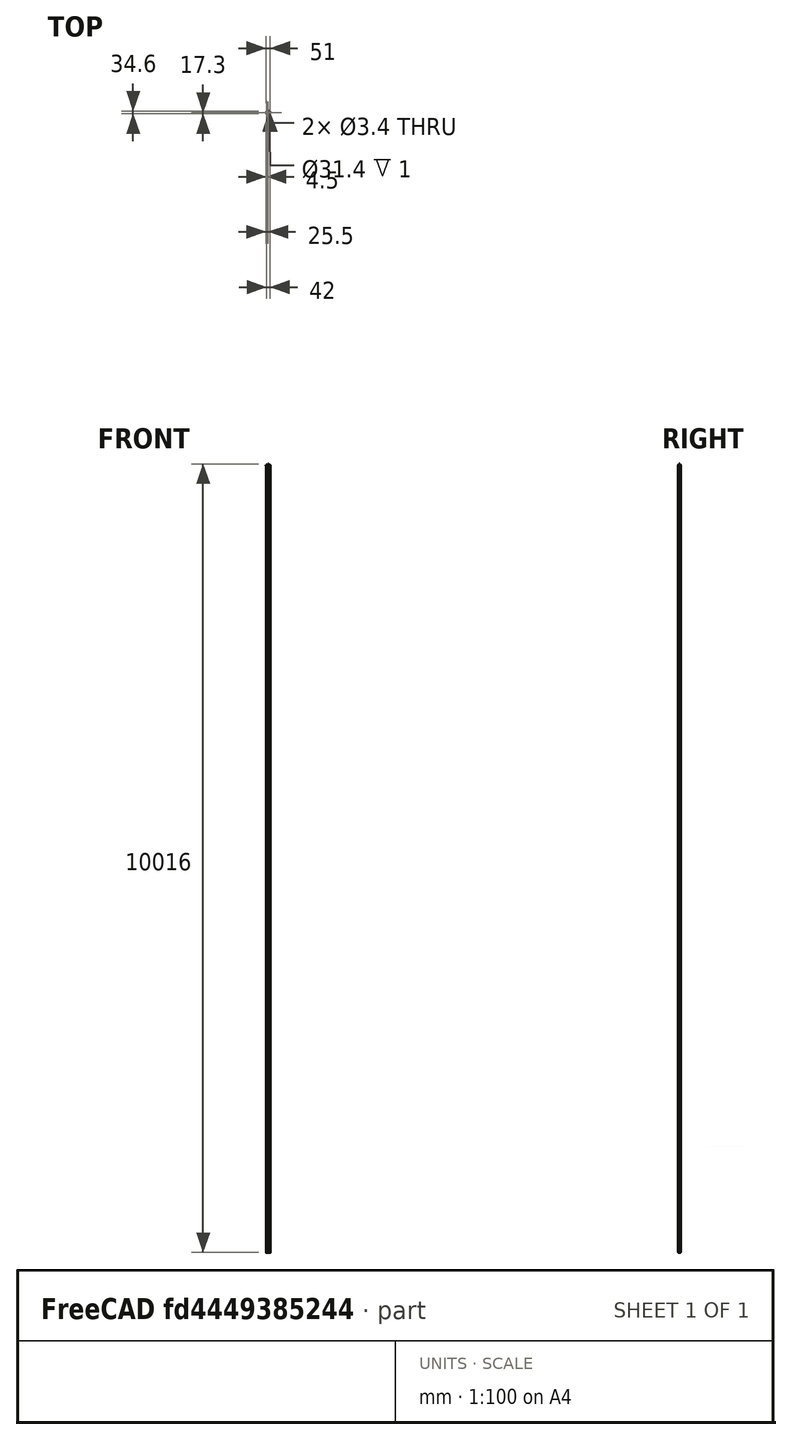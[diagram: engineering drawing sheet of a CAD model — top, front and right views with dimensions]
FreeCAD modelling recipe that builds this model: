
FCSTD DOCUMENT  (FreeCAD 0.15R4671 (Git))
Label: Small Stepper Test Frame
License: All rights reserved
LicenseURL: http://en.wikipedia.org/wiki/All_rights_reserved
objects: Sketcher::SketchObject×7, PartDesign::Pocket×4, PartDesign::Pad×3, Mesh::Feature×1
note: 21 computed .brp shape members not serialized (recipe doc carries the construction recipe); baked Part::Feature solids carry a one-line shape summary decoded from their .brp

FEATURE [Sketcher::SketchObject] Sketch
  sketch-geometry (11):
    g0: Circle [constr] CenterX=0 CenterY=0 CenterZ=0 NormalX=0 NormalY=0 NormalZ=1 Radius=13.5
    g1: Circle [constr] CenterX=-21 CenterY=0 CenterZ=0 NormalX=0 NormalY=0 NormalZ=1 Radius=4.5
    g2: Circle [constr] CenterX=21 CenterY=0 CenterZ=0 NormalX=0 NormalY=0 NormalZ=1 Radius=4.5
    g3: LineSegment StartX=-22.9286 StartY=4.06578 StartZ=0 EndX=-5.78572 EndY=12.1974 EndZ=0
    g4: LineSegment StartX=5.78572 StartY=12.1974 StartZ=0 EndX=22.9286 EndY=4.06578 EndZ=0
    g5: LineSegment StartX=22.9286 StartY=-4.06578 StartZ=0 EndX=5.78572 EndY=-12.1974 EndZ=0
    g6: LineSegment StartX=-5.78572 StartY=-12.1974 StartZ=0 EndX=-22.9286 EndY=-4.06578 EndZ=0
    g7: ArcOfCircle CenterX=-21 CenterY=0 CenterZ=0 NormalX=0 NormalY=0 NormalZ=1 Radius=4.5 StartAngle=2.01371 EndAngle=4.26947
    g8: ArcOfCircle CenterX=0 CenterY=0 CenterZ=0 NormalX=0 NormalY=0 NormalZ=1 Radius=13.5 StartAngle=1.12788 EndAngle=2.01371
    g9: ArcOfCircle CenterX=21 CenterY=0 CenterZ=0 NormalX=0 NormalY=0 NormalZ=1 Radius=4.5 StartAngle=5.15531 EndAngle=7.41107
    g10: ArcOfCircle CenterX=0 CenterY=0 CenterZ=0 NormalX=0 NormalY=0 NormalZ=1 Radius=13.5 StartAngle=4.26948 EndAngle=5.1553
  constraints (36):
    c: Coincident(g0,g-1)
    c: PointOnObject(g1,g-1)
    c: PointOnObject(g2,g-1)
    c: Symmetric(g1,g2,g-2)
    c: Equal(g1,g2)
    c: Radius(g0) = 13.5
    c: DistanceX(g1,g2) = 42
    c: Radius(g2) = 4.5
    c: PointOnObject(g3,g1)
    c: PointOnObject(g3,g0)
    c: Tangent(g3,g1)
    c: PointOnObject(g4,g0)
    c: PointOnObject(g4,g2)
    c: Tangent(g4,g2)
    c: PointOnObject(g5,g2)
    c: Tangent(g5,g0)
    c: PointOnObject(g6,g0)
    c: PointOnObject(g6,g1)
    c: Tangent(g6,g1)
    c: Tangent(g3,g0)
    c: Tangent(g4,g0)
    c: Tangent(g5,g2)
    c: Tangent(g6,g0)
    c: PointOnObject(g5,g0)
    c: Coincident(g7,g1)
    c: Coincident(g7,g3)
    c: Coincident(g7,g6)
    c: Coincident(g8,g-1)
    c: Coincident(g8,g3)
    c: Coincident(g8,g4)
    c: Coincident(g9,g2)
    c: Coincident(g9,g4)
    c: Coincident(g9,g5)
    c: Coincident(g10,g-1)
    c: Coincident(g10,g5)
    c: Coincident(g10,g6)
FEATURE [PartDesign::Pad] Pad
  Length = 2
  Length2 = 100
  Sketch = -> Sketch
  Type = 0
FEATURE [Sketcher::SketchObject] Sketch001
  Placement = pos=(0,0,2) rot=(0,0,1;0rad)
  Support = -> Pad [Face10]
  sketch-geometry (11):
    g0: Circle [constr] CenterX=0 CenterY=0 CenterZ=0 NormalX=0 NormalY=0 NormalZ=1 Radius=12.7
    g1: Circle [constr] CenterX=-21 CenterY=0 CenterZ=0 NormalX=0 NormalY=0 NormalZ=1 Radius=3.7
    g2: Circle [constr] CenterX=21 CenterY=0 CenterZ=0 NormalX=0 NormalY=0 NormalZ=1 Radius=3.7
    g3: LineSegment StartX=-22.5857 StartY=3.34297 StartZ=0 EndX=-5.44286 EndY=11.4745 EndZ=0
    g4: LineSegment StartX=5.44286 StartY=11.4745 StartZ=0 EndX=22.5857 EndY=3.34297 EndZ=0
    g5: LineSegment StartX=22.5857 StartY=-3.34297 StartZ=0 EndX=5.44286 EndY=-11.4745 EndZ=0
    g6: LineSegment StartX=-5.44286 StartY=-11.4745 StartZ=0 EndX=-22.5857 EndY=-3.34297 EndZ=0
    g7: ArcOfCircle CenterX=-21 CenterY=0 CenterZ=0 NormalX=0 NormalY=0 NormalZ=1 Radius=3.7 StartAngle=2.01371 EndAngle=4.26947
    g8: ArcOfCircle CenterX=0 CenterY=0 CenterZ=0 NormalX=0 NormalY=0 NormalZ=1 Radius=12.7 StartAngle=1.12788 EndAngle=2.01371
    g9: ArcOfCircle CenterX=21 CenterY=0 CenterZ=0 NormalX=0 NormalY=0 NormalZ=1 Radius=3.7 StartAngle=5.1553 EndAngle=7.41107
    g10: ArcOfCircle CenterX=0 CenterY=0 CenterZ=0 NormalX=0 NormalY=0 NormalZ=1 Radius=12.7 StartAngle=4.26948 EndAngle=5.1553
  constraints (36):
    c: Coincident(g0,g-1)
    c: PointOnObject(g1,g-1)
    c: PointOnObject(g2,g-1)
    c: Symmetric(g1,g2,g-2)
    c: Equal(g1,g2)
    c: Radius(g0) = 12.7
    c: DistanceX(g1,g2) = 42
    c: Radius(g2) = 3.7
    c: PointOnObject(g3,g1)
    c: PointOnObject(g3,g0)
    c: Tangent(g3,g1)
    c: PointOnObject(g4,g0)
    c: PointOnObject(g4,g2)
    c: Tangent(g4,g2)
    c: PointOnObject(g5,g2)
    c: Tangent(g5,g0)
    c: PointOnObject(g6,g0)
    c: PointOnObject(g6,g1)
    c: Tangent(g6,g1)
    c: Tangent(g3,g0)
    c: Tangent(g4,g0)
    c: Tangent(g5,g2)
    c: Tangent(g6,g0)
    c: PointOnObject(g5,g0)
    c: Coincident(g7,g1)
    c: Coincident(g7,g3)
    c: Coincident(g7,g6)
    c: Coincident(g8,g-1)
    c: Coincident(g8,g3)
    c: Coincident(g8,g4)
    c: Coincident(g9,g2)
    c: Coincident(g9,g4)
    c: Coincident(g9,g5)
    c: Coincident(g10,g-1)
    c: Coincident(g10,g5)
    c: Coincident(g10,g6)
FEATURE [PartDesign::Pocket] Pocket
  Length = 1
  Sketch = -> Sketch001
  Type = 0
FEATURE [Sketcher::SketchObject] Sketch002
  Placement = pos=(0,0,1) rot=(0,0,1;0rad)
  Support = -> Pocket [Face19]
  sketch-geometry (11):
    g0: Circle [constr] CenterX=0 CenterY=0 CenterZ=0 NormalX=0 NormalY=0 NormalZ=1 Radius=11.7
    g1: Circle [constr] CenterX=-21 CenterY=0 CenterZ=0 NormalX=0 NormalY=0 NormalZ=1 Radius=2.7
    g2: Circle [constr] CenterX=21 CenterY=0 CenterZ=0 NormalX=0 NormalY=0 NormalZ=1 Radius=2.7
    g3: LineSegment StartX=-22.1571 StartY=2.43947 StartZ=0 EndX=-5.01426 EndY=10.5711 EndZ=0
    g4: LineSegment StartX=5.01426 StartY=10.5711 StartZ=0 EndX=22.1571 EndY=2.43947 EndZ=0
    g5: LineSegment StartX=22.1571 StartY=-2.43947 StartZ=0 EndX=5.01426 EndY=-10.5711 EndZ=0
    g6: LineSegment StartX=-5.01426 StartY=-10.5711 StartZ=0 EndX=-22.1571 EndY=-2.43947 EndZ=0
    g7: ArcOfCircle CenterX=-21 CenterY=0 CenterZ=0 NormalX=0 NormalY=0 NormalZ=1 Radius=2.7 StartAngle=2.01371 EndAngle=4.26948
    g8: ArcOfCircle CenterX=0 CenterY=0 CenterZ=0 NormalX=0 NormalY=0 NormalZ=1 Radius=11.7 StartAngle=1.12789 EndAngle=2.01371
    g9: ArcOfCircle CenterX=21 CenterY=0 CenterZ=0 NormalX=0 NormalY=0 NormalZ=1 Radius=2.7 StartAngle=5.1553 EndAngle=7.41107
    g10: ArcOfCircle CenterX=0 CenterY=0 CenterZ=0 NormalX=0 NormalY=0 NormalZ=1 Radius=11.7 StartAngle=4.26948 EndAngle=5.1553
  constraints (36):
    c: Coincident(g0,g-1)
    c: PointOnObject(g1,g-1)
    c: PointOnObject(g2,g-1)
    c: Symmetric(g1,g2,g-2)
    c: Equal(g1,g2)
    c: Radius(g0) = 11.7
    c: DistanceX(g1,g2) = 42
    c: Radius(g2) = 2.7
    c: PointOnObject(g3,g1)
    c: PointOnObject(g3,g0)
    c: Tangent(g3,g1)
    c: PointOnObject(g4,g0)
    c: PointOnObject(g4,g2)
    c: Tangent(g4,g2)
    c: PointOnObject(g5,g2)
    c: Tangent(g5,g0)
    c: PointOnObject(g6,g0)
    c: PointOnObject(g6,g1)
    c: Tangent(g6,g1)
    c: Tangent(g3,g0)
    c: Tangent(g4,g0)
    c: Tangent(g5,g2)
    c: Tangent(g6,g0)
    c: PointOnObject(g5,g0)
    c: Coincident(g7,g1)
    c: Coincident(g7,g3)
    c: Coincident(g7,g6)
    c: Coincident(g8,g-1)
    c: Coincident(g8,g3)
    c: Coincident(g8,g4)
    c: Coincident(g9,g2)
    c: Coincident(g9,g4)
    c: Coincident(g9,g5)
    c: Coincident(g10,g-1)
    c: Coincident(g10,g5)
    c: Coincident(g10,g6)
FEATURE [PartDesign::Pocket] Pocket001
  Length = 5
  Sketch = -> Sketch002
  Type = 1
FEATURE [Sketcher::SketchObject] Sketch003
  sketch-geometry (14):
    g0: Circle [constr] CenterX=0 CenterY=0 CenterZ=0 NormalX=0 NormalY=0 NormalZ=1 Radius=17.3
    g1: Circle [constr] CenterX=-21 CenterY=0 CenterZ=0 NormalX=0 NormalY=0 NormalZ=1 Radius=3.3
    g2: Circle [constr] CenterX=21 CenterY=0 CenterZ=0 NormalX=0 NormalY=0 NormalZ=1 Radius=3.3
    g3: LineSegment StartX=-23.2 StartY=2.45967 StartZ=0 EndX=-11.5333 EndY=12.8947 EndZ=0
    g4: LineSegment StartX=11.5333 StartY=12.8947 StartZ=0 EndX=23.2 EndY=2.45968 EndZ=0
    g5: LineSegment StartX=23.2 StartY=-2.45968 StartZ=0 EndX=11.5333 EndY=-12.8947 EndZ=0
    g6: LineSegment StartX=-11.5333 StartY=-12.8947 StartZ=0 EndX=-23.2 EndY=-2.45967 EndZ=0
    g7: ArcOfCircle CenterX=-21 CenterY=0 CenterZ=0 NormalX=0 NormalY=0 NormalZ=1 Radius=3.3 StartAngle=2.30052 EndAngle=3.98266
    g8: ArcOfCircle CenterX=0 CenterY=0 CenterZ=0 NormalX=0 NormalY=0 NormalZ=1 Radius=17.3 StartAngle=0.841069 EndAngle=2.30052
    g9: ArcOfCircle CenterX=21 CenterY=0 CenterZ=0 NormalX=0 NormalY=0 NormalZ=1 Radius=3.3 StartAngle=5.44211 EndAngle=7.12426
    g10: ArcOfCircle CenterX=0 CenterY=0 CenterZ=0 NormalX=0 NormalY=0 NormalZ=1 Radius=17.3 StartAngle=3.98266 EndAngle=5.44212
    g11: Circle CenterX=-21 CenterY=0 CenterZ=0 NormalX=0 NormalY=0 NormalZ=1 Radius=1.7
    g12: Circle CenterX=21 CenterY=0 CenterZ=0 NormalX=0 NormalY=0 NormalZ=1 Radius=1.7
    g13: Circle CenterX=0 CenterY=0 CenterZ=0 NormalX=0 NormalY=0 NormalZ=1 Radius=15.7
  constraints (42):
    c: Coincident(g0,g-1)
    c: PointOnObject(g1,g-1)
    c: PointOnObject(g2,g-1)
    c: Symmetric(g1,g2,g-2)
    c: Equal(g1,g2)
    c: Radius(g0) = 17.3
    c: DistanceX(g1,g2) = 42
    c: Radius(g2) = 3.3
    c: PointOnObject(g3,g1)
    c: PointOnObject(g3,g0)
    c: PointOnObject(g4,g0)
    c: PointOnObject(g4,g2)
    c: Tangent(g4,g2)
    c: PointOnObject(g5,g2)
    c: Tangent(g5,g0)
    c: PointOnObject(g6,g0)
    c: PointOnObject(g6,g1)
    c: Tangent(g3,g0)
    c: Tangent(g4,g0)
    c: Tangent(g5,g2)
    c: Tangent(g6,g0)
    c: PointOnObject(g5,g0)
    c: Coincident(g7,g1)
    c: Coincident(g7,g3)
    c: Coincident(g7,g6)
    c: Coincident(g8,g-1)
    c: Coincident(g8,g3)
    c: Coincident(g8,g4)
    c: Coincident(g9,g2)
    c: Coincident(g9,g4)
    c: Coincident(g9,g5)
    c: Coincident(g10,g-1)
    c: Coincident(g10,g5)
    c: Coincident(g10,g6)
    c: Coincident(g11,g1)
    c: Coincident(g12,g2)
    c: Equal(g12,g11)
    c: Radius(g12) = 1.7
    c: Coincident(g13,g-1)
    c: Radius(g13) = 15.7
    c: Tangent(g1,g3)
    c: Tangent(g6,g1)
FEATURE [PartDesign::Pad] Pad001
  Length = 1
  Length2 = 100
  Sketch = -> Sketch003
  Type = 0
FEATURE [Mesh::Feature] Small_Stepper  label="Small Stepper"
FEATURE [Sketcher::SketchObject] Sketch004
  sketch-geometry (1):
    g0: Circle CenterX=0 CenterY=0 CenterZ=0 NormalX=0 NormalY=0 NormalZ=1 Radius=4
  constraints (2):
    c: Coincident(g0,g-1)
    c: Radius(g0) = 4
FEATURE [PartDesign::Pad] Pad002
  Length = 17
  Length2 = 100
  Sketch = -> Sketch004
  Type = 0
FEATURE [Sketcher::SketchObject] Sketch005
  Placement = pos=(0,0,17) rot=(0,0,1;0rad)
  Support = -> Pad002 [Face3]
  sketch-geometry (1):
    g0: Circle CenterX=0 CenterY=0 CenterZ=0 NormalX=0 NormalY=0 NormalZ=1 Radius=1.5
  constraints (2):
    c: Coincident(g0,g-1)
    c: Radius(g0) = 1.5
FEATURE [PartDesign::Pocket] Pocket002
  Length = 8
  Sketch = -> Sketch005
  Type = 0
FEATURE [Sketcher::SketchObject] Sketch006
  Placement = pos=(0,0,0) rot=(1,0,0;3.14159rad)
  Support = -> Pocket002 [Face2]
  sketch-geometry (12):
    g0: LineSegment StartX=-0.95 StartY=2.5 StartZ=0 EndX=0.95 EndY=2.5 EndZ=0
    g1: LineSegment StartX=0.95 StartY=2.5 StartZ=0 EndX=0.95 EndY=0.95 EndZ=0
    g2: LineSegment StartX=0.95 StartY=0.95 StartZ=0 EndX=2.5 EndY=0.95 EndZ=0
    g3: LineSegment StartX=2.5 StartY=0.95 StartZ=0 EndX=2.5 EndY=-0.95 EndZ=0
    g4: LineSegment StartX=2.5 StartY=-0.95 StartZ=0 EndX=0.95 EndY=-0.95 EndZ=0
    g5: LineSegment StartX=0.95 StartY=-0.95 StartZ=0 EndX=0.95 EndY=-2.5 EndZ=0
    g6: LineSegment StartX=0.95 StartY=-2.5 StartZ=0 EndX=-0.95 EndY=-2.5 EndZ=0
    g7: LineSegment StartX=-0.95 StartY=-2.5 StartZ=0 EndX=-0.95 EndY=-0.95 EndZ=0
    g8: LineSegment StartX=-0.95 StartY=-0.95 StartZ=0 EndX=-2.5 EndY=-0.95 EndZ=0
    g9: LineSegment StartX=-2.5 StartY=-0.95 StartZ=0 EndX=-2.5 EndY=0.95 EndZ=0
    g10: LineSegment StartX=-2.5 StartY=0.95 StartZ=0 EndX=-0.95 EndY=0.95 EndZ=0
    g11: LineSegment StartX=-0.95 StartY=0.95 StartZ=0 EndX=-0.95 EndY=2.5 EndZ=0
  constraints (38):
    c: Horizontal(g0)
    c: Coincident(g0,g1)
    c: Vertical(g1)
    c: Coincident(g1,g2)
    c: Horizontal(g2)
    c: Coincident(g2,g3)
    c: Vertical(g3)
    c: Coincident(g3,g4)
    c: Horizontal(g4)
    c: Coincident(g4,g5)
    c: Vertical(g5)
    c: Coincident(g5,g6)
    c: Horizontal(g6)
    c: Coincident(g6,g7)
    c: Vertical(g7)
    c: Coincident(g7,g8)
    c: Horizontal(g8)
    c: Coincident(g8,g9)
    c: Vertical(g9)
    c: Coincident(g9,g10)
    c: Horizontal(g10)
    c: Coincident(g10,g11)
    c: Coincident(g11,g0)
    c: Vertical(g11)
    c: Equal(g10,g11)
    c: Equal(g11,g1)
    c: Equal(g1,g2)
    c: Equal(g2,g4)
    c: Equal(g4,g5)
    c: Equal(g5,g7)
    c: Equal(g7,g8)
    c: Equal(g0,g9)
    c: Equal(g9,g3)
    c: Equal(g3,g6)
    c: Symmetric(g10,g1,g-2)
    c: Symmetric(g7,g10,g-1)
    c: DistanceY(g0,g5) = -5
    c: DistanceY(g9,g8) = -1.9
FEATURE [PartDesign::Pocket] Pocket003
  Length = 8
  Sketch = -> Sketch006
  Type = 0
